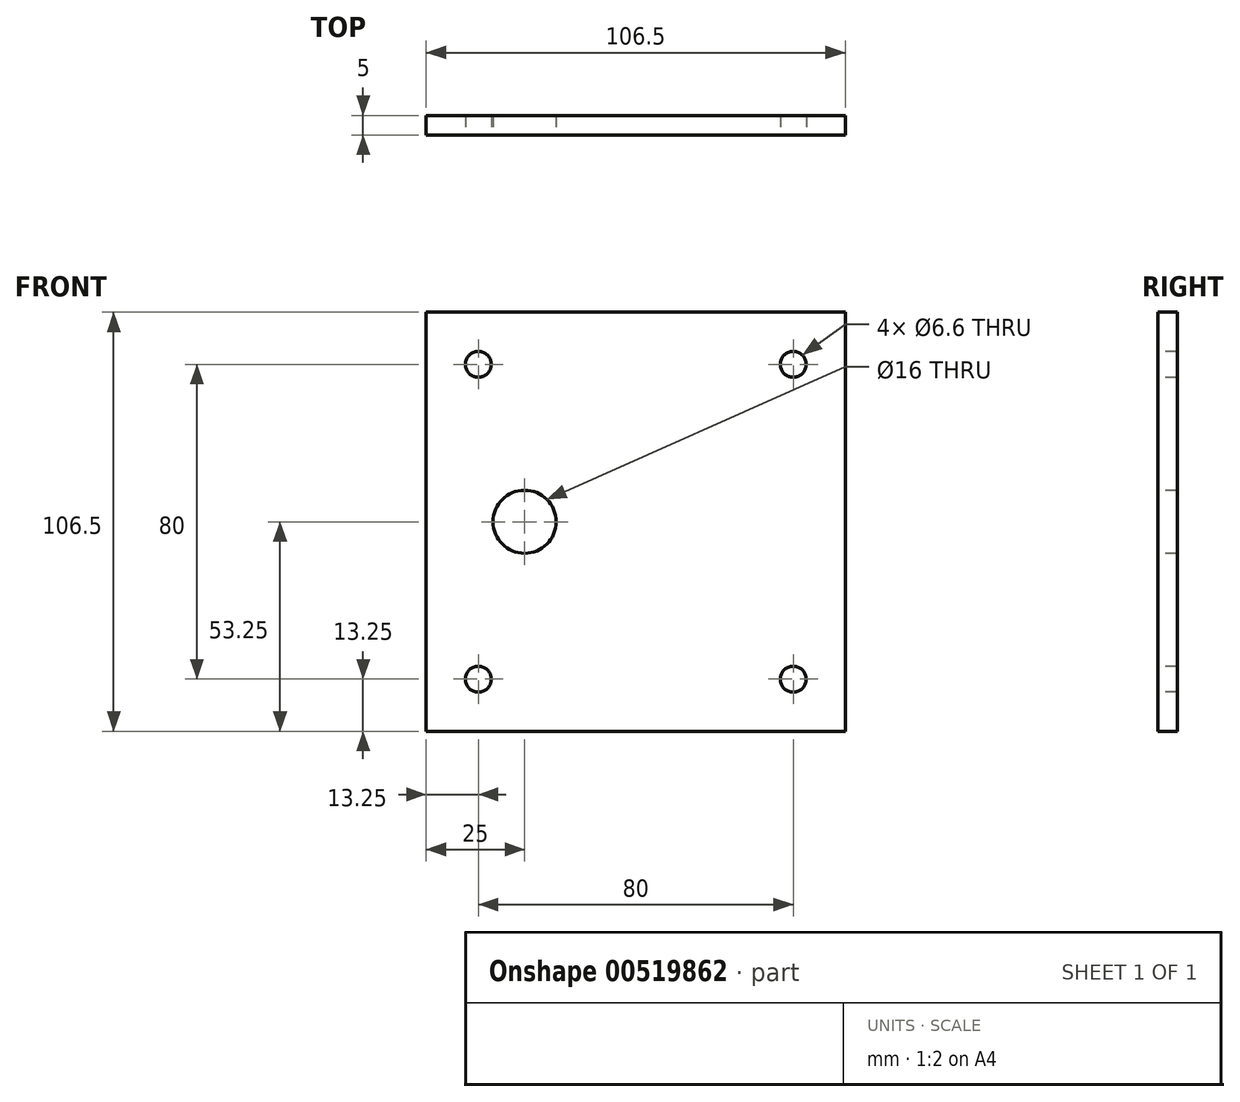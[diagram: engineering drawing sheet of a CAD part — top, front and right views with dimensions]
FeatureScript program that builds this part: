
annotation { "Feature Type Name" : "Feature", "Feature Type Description" : "" }
export const myFeature = defineFeature(function(context is Context, id is Id, definition is map)
    precondition{}
    {
        {
            var Q0;
            Q0=qCreatedBy(makeId("Front.planeOp"),FACE);
            var sketch = newSketch(context, id + "F0", { "sketchPlane" : qUnion([Q0])});
            skLineSegment(sketch, "E0.bottom", {"start": v(0, 0) * mm, "end": v(-106.5, 0) * mm});
            skLineSegment(sketch, "E0.top", {"start": v(0, 106.5) * mm, "end": v(-106.5, 106.5) * mm});
            skLineSegment(sketch, "E0.left", {"start": v(0, 0) * mm, "end": v(0, 106.5) * mm});
            skLineSegment(sketch, "E0.right", {"start": v(-106.5, 0) * mm, "end": v(-106.5, 106.5) * mm});
            skSolve(sketch);
        }
        {
            var Q0;
            Q0=makeQuery(id+"F0.imprint","IMPRINT",FACE,{"disambiguationData":[TD([[makeQuery(id+"F0.imprint","IMPRINT",EDGE,{"derivedFrom":sQuery(id+"F0.wireOp",EDGE,"E0.bottom")}),-1.0]])]});
            extrude(context, id + "F1", {"entities" : qUnion([Q0]), "depth" : 5 * mm, "offsetDistance" : 25 * mm});
        }
        {
            var Q0;
            Q0=makeQuery(id+"F1.opExtrude","CAP_FACE",FACE,{"disambiguationData":[OSD([sQuery(id+"F0.wireOp",EDGE,"E0.bottom"),sQuery(id+"F0.wireOp",EDGE,"E0.top"),sQuery(id+"F0.wireOp",EDGE,"E0.left"),sQuery(id+"F0.wireOp",EDGE,"E0.right")])],"isStart":false});
            var sketch = newSketch(context, id + "F2", { "sketchPlane" : qUnion([Q0])});
            skLineSegment(sketch, "E1", {"start": v(-106.5, 106.5) * mm, "end": v(-106.5, 0) * mm});
            skLineSegment(sketch, "E2", {"start": v(-53.25, 53.25) * mm, "end": v(-13.25, 53.25) * mm});
            skLineSegment(sketch, "E3", {"start": v(-13.25, 53.25) * mm, "end": v(-13.25, 93.25) * mm});
            skLineSegment(sketch, "E4", {"start": v(-13.25, 53.25) * mm, "end": v(-13.25, 13.25) * mm});
            skLineSegment(sketch, "E5", {"start": v(-93.25, 53.25) * mm, "end": v(-93.25, 93.25) * mm});
            skLineSegment(sketch, "E6", {"start": v(-93.25, 53.25) * mm, "end": v(-93.25, 13.25) * mm});
            skLineSegment(sketch, "E7", {"start": v(-53.25, 53.25) * mm, "end": v(-53.25, 106.5) * mm});
            skLineSegment(sketch, "E8", {"start": v(-53.25, 106.5) * mm, "end": v(0, 106.5) * mm});
            skLineSegment(sketch, "E9", {"start": v(-93.25, 53.25) * mm, "end": v(-83.25, 53.25) * mm});
            skSolve(sketch);
        }
        {
            var Q0;
            Q0=sQuery(id+"F2.wireOp",VERTEX,"E5.end");
            var Q1;
            Q1=sQuery(id+"F2.wireOp",VERTEX,"E6.end");
            var Q2;
            Q2=sQuery(id+"F2.wireOp",VERTEX,"E4.end");
            var Q3;
            Q3=sQuery(id+"F2.wireOp",VERTEX,"E3.end");
            var Q4;
            Q4=makeQuery(id+"F1.opExtrude","SWEPT_BODY",BODY,{"disambiguationData":[OSD([sQuery(id+"F0.wireOp",EDGE,"E0.bottom"),sQuery(id+"F0.wireOp",EDGE,"E0.top"),sQuery(id+"F0.wireOp",EDGE,"E0.left"),sQuery(id+"F0.wireOp",EDGE,"E0.right")])]});
            hole(context, id + "F3", {"style" : HoleStyle.SIMPLE, "endStyle" : HoleEndStyle.THROUGH, "standardTappedOrClearance" : lookupTablePath({ "standard" : "ISO", "fit" : "Normal", "size" : "M6", "type" : "Clearance" }), "standardBlindInLast" : lookupTablePath({ "fit" : "Standard", "standard" : "ISO", "size" : "M6", "type" : "Clearance" }), "holeDiameter" : 6.6 * mm, "isTappedThrough" : true, "tappedDepth" : 12 * mm, "tapClearance" : 3, "locations" : qUnion([Q0, Q1, Q2, Q3]), "scope" : qUnion([Q4])});
        }
        {
            var Q0;
            Q0=makeQuery(id+"F1.opExtrude","CAP_FACE",FACE,{"disambiguationData":[OSD([sQuery(id+"F0.wireOp",EDGE,"E0.bottom"),sQuery(id+"F0.wireOp",EDGE,"E0.top"),sQuery(id+"F0.wireOp",EDGE,"E0.left"),sQuery(id+"F0.wireOp",EDGE,"E0.right")])],"isStart":false});
            var sketch = newSketch(context, id + "F4", { "sketchPlane" : qUnion([Q0])});
            skLineSegment(sketch, "E10", {"start": v(-106.5, 53.25) * mm, "end": v(-81.5, 53.25) * mm});
            skSolve(sketch);
        }
        {
            var Q0;
            Q0=sQuery(id+"F4.wireOp",VERTEX,"E10.end");
            var Q1;
            Q1=makeQuery(id+"F1.opExtrude","SWEPT_BODY",BODY,{"disambiguationData":[OSD([sQuery(id+"F0.wireOp",EDGE,"E0.bottom"),sQuery(id+"F0.wireOp",EDGE,"E0.top"),sQuery(id+"F0.wireOp",EDGE,"E0.left"),sQuery(id+"F0.wireOp",EDGE,"E0.right")])]});
            hole(context, id + "F5", {"style" : HoleStyle.SIMPLE, "endStyle" : HoleEndStyle.THROUGH, "holeDiameter" : 16 * mm, "isTappedThrough" : true, "tappedDepth" : 12 * mm, "tapClearance" : 3, "locations" : qUnion([Q0]), "scope" : qUnion([Q1])});
        }
    });
